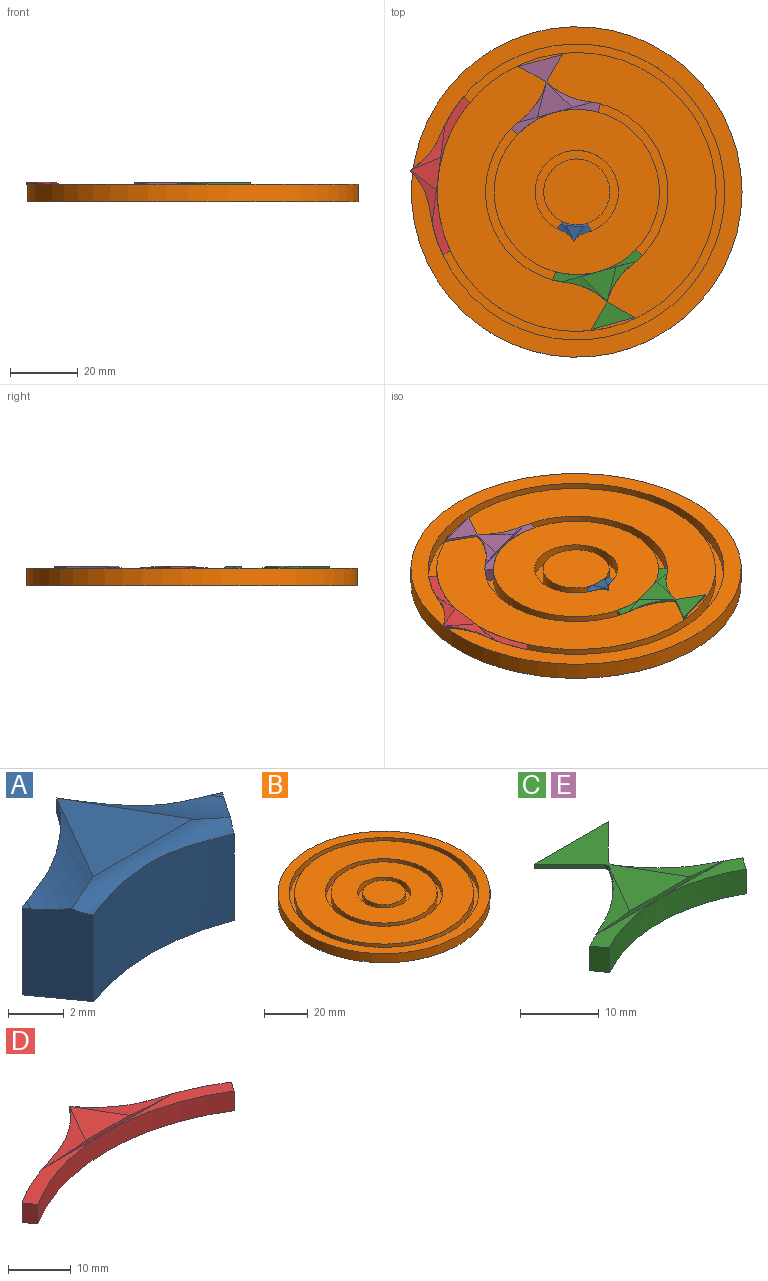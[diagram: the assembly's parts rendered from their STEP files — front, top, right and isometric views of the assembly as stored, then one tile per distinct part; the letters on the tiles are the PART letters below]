
ASSEMBLY  parts=5 mates=4
PART A: 16 faces, bbox 10.4x6.7x4.5 mm
  f0: plane 0.06x0.02mm, normal (0,0,1), area 0mm2, adj f4,f5,f15
  f1: plane 0.06x0.02mm, normal (0,0,1), area 0mm2, adj f3,f4,f15
  f2: plane 0.43x0.43mm, normal (0,0,1), area 0.1mm2, adj f5,f6,f12
  f3: plane 4.02x2.13mm, normal (-0.81,-0.59,0), area 10.1mm2, adj f1,f4,f6,f7,f8,f11,f15
  f4: cylinder r=9.75mm len=7.11mm, axis (0,0,-1), area 28.5mm2, adj f0,f1,f3,f5,f8,f15
  f5: plane 4.02x2.13mm, normal (0.81,-0.59,0), area 10.1mm2, adj f0,f2,f4,f6,f8,f12,f15
  f6: cylinder r=12.29mm len=10.16mm, axis (0,0,-1), area 40mm2, adj f2,f3,f5,f7,f8,f9,f11,f12
  f7: plane 0.43x0.43mm, normal (0,0,1), area 0.1mm2, adj f3,f6,f11
  f8: plane 10.16x3.21mm, normal (0,0,-1), area 22.6mm2, adj f3,f4,f5,f6
  f9: plane 7.33x2.78mm, normal (0,0,-1), area 5mm2, adj f6,f13,f14
  f10: plane 5.06x4.38mm, normal (0,0,1), area 11.1mm2, adj f11,f12,f15
  f11: cylinder r=5.08mm len=6.56mm, axis (-0.5,-0.87,0), area 6.3mm2, adj f3,f6,f7,f10,f13,f15
  f12: cylinder r=5.08mm len=6.56mm, axis (-0.5,0.87,0), area 6.3mm2, adj f2,f5,f6,f10,f14,f15
  f13: cylinder r=6.78mm len=3.67mm, axis (0,0,-1), area 1.7mm2, adj f6,f9,f11,f14
  f14: cylinder r=6.78mm len=3.67mm, axis (0,0,1), area 1.7mm2, adj f6,f9,f12,f13
  f15: cylinder r=1.17mm len=8.05mm, axis (1,0,0), area 5.9mm2, adj f0,f1,f3,f4,f5,f10,f11,f12
PART B: 15 faces, bbox 97.5x97.5x5.1 mm
  f0: cylinder r=48.77mm len=97.54mm, axis (0,0,-1), area 1556.6mm2, adj f1,f2
  f1: plane 97.54x97.54mm, normal (0,0,1), area 1475.5mm2, adj f0,f4
  f2: plane 97.54x97.54mm, normal (0,0,-1), area 7471.7mm2, adj f0
  f3: cylinder r=41.15mm len=82.3mm, axis (0,0,1), area 985mm2, adj f5,f6
  f4: cylinder r=43.69mm len=87.38mm, axis (0,0,1), area 1045.8mm2, adj f1,f5
  f5: plane 87.38x87.38mm, normal (0,0,1), area 677mm2, adj f3,f4
  f6: plane 82.3x82.3mm, normal (0,0,1), area 3041.9mm2, adj f3,f8
  f7: cylinder r=24.38mm len=48.77mm, axis (0,0,1), area 583.7mm2, adj f9,f10
  f8: cylinder r=26.92mm len=53.85mm, axis (0,0,1), area 644.5mm2, adj f6,f9
  f9: plane 53.85x53.85mm, normal (0,0,1), area 409.4mm2, adj f7,f8
  f10: plane 48.77x48.77mm, normal (0,0,1), area 1393.1mm2, adj f7,f12
  f11: cylinder r=9.75mm len=19.51mm, axis (0,0,1), area 233.5mm2, adj f13,f14
  f12: cylinder r=12.29mm len=24.59mm, axis (0,0,1), area 294.3mm2, adj f10,f13
  f13: plane 24.59x24.59mm, normal (0,0,1), area 175.9mm2, adj f11,f12
  f14: plane 19.51x19.51mm, normal (0,0,1), area 298.9mm2, adj f11
PART C: 19 faces, bbox 27.4x19.2x4.5 mm
  f0: cylinder r=20.82mm len=9.89mm, axis (0,0,-1), area 5.7mm2, adj f6,f9,f12,f14
  f1: cylinder r=20.82mm len=9.89mm, axis (0,0,1), area 5.7mm2, adj f6,f9,f13,f15
  f2: plane 13.72x3.29mm, normal (0,0,1), area 15mm2, adj f4,f5,f6,f10
  f3: plane 3.81x2.07mm, normal (-0.81,-0.59,0), area 9.7mm2, adj f4,f6,f7,f8
  f4: cylinder r=24.38mm len=24.45mm, axis (0,0,-1), area 97.6mm2, adj f2,f3,f5,f7,f8
  f5: plane 3.81x2.07mm, normal (0.81,-0.59,0), area 9.7mm2, adj f2,f4,f6,f8
  f6: cylinder r=26.92mm len=27.43mm, axis (0,0,-1), area 110mm2, adj f0,f1,f2,f3,f5,f7,f8,f9
  f7: plane 13.72x3.29mm, normal (0,0,1), area 15mm2, adj f3,f4,f6,f10
  f8: plane 27.43x5.83mm, normal (0,0,-1), area 69.1mm2, adj f3,f4,f5,f6
  f9: plane 20.2x15.32mm, normal (0,0,-1), area 85.6mm2, adj f0,f1,f6,f14,f15,f16,f17,f18
  f10: plane 22.84x0.64mm, normal (0,-1,0), area 10.6mm2, adj f2,f6,f7,f11,f12,f13
  f11: plane 15.88x13.29mm, normal (0,0,1), area 93.6mm2, adj f10,f12,f13,f14,f15,f16,f17,f18
  f12: cylinder r=53.59mm len=14.17mm, axis (-0.5,-0.87,0), area 15.7mm2, adj f0,f6,f10,f11
  f13: cylinder r=53.59mm len=14.17mm, axis (-0.5,0.87,0), area 15.7mm2, adj f1,f6,f10,f11
  f14: plane 0.64x0.64mm, normal (-0.99,-0.17,0), area 0.4mm2, adj f0,f9,f11,f18
  f15: plane 0.64x0.64mm, normal (0.99,-0.17,0), area 0.4mm2, adj f1,f9,f11,f16
  f16: plane 6.34x6.34mm, normal (0.71,-0.71,0), area 5.7mm2, adj f9,f11,f15,f17
  f17: plane 13.29x0.64mm, normal (0,1,0), area 8.4mm2, adj f9,f11,f16,f18
  f18: plane 6.34x6.34mm, normal (-0.71,-0.71,0), area 5.7mm2, adj f9,f11,f14,f17
PART D: 14 faces, bbox 47.1x19x4.5 mm
  f0: plane 23.55x6.54mm, normal (0,0,1), area 36.2mm2, adj f1,f2,f4,f8,f10
  f1: plane 3.81x2.06mm, normal (-0.81,-0.59,0), area 9.7mm2, adj f0,f2,f4,f6
  f2: cylinder r=41.15mm len=44.12mm, axis (0,0,-1), area 177.4mm2, adj f0,f1,f3,f5,f6
  f3: plane 3.81x2.06mm, normal (0.81,-0.59,0), area 9.7mm2, adj f2,f4,f5,f6
  f4: cylinder r=43.69mm len=47.1mm, axis (0,0,-1), area 189.6mm2, adj f0,f1,f3,f5,f6,f7,f10,f11
  f5: plane 23.55x6.54mm, normal (0,0,1), area 36.2mm2, adj f2,f3,f4,f8,f11
  f6: plane 47.1x8.95mm, normal (0,0,-1), area 122.3mm2, adj f1,f2,f3,f4
  f7: plane 22.32x7.4mm, normal (0,0,-1), area 41.1mm2, adj f4,f12,f13
  f8: plane 28.82x0.65mm, normal (0,-1,0), area 10.2mm2, adj f0,f5,f9,f10,f11
  f9: plane 9.81x8.49mm, normal (0,0,1), area 41.7mm2, adj f8,f10,f11
  f10: cylinder r=53.59mm len=16.72mm, axis (-0.5,-0.87,0), area 24.9mm2, adj f0,f4,f8,f9,f12
  f11: cylinder r=53.59mm len=16.72mm, axis (-0.5,0.87,0), area 24.9mm2, adj f4,f5,f8,f9,f13
  f12: cylinder r=20.82mm len=11.16mm, axis (0,0,-1), area 4.8mm2, adj f4,f7,f10,f13
  f13: cylinder r=20.82mm len=11.16mm, axis (0,0,1), area 4.8mm2, adj f4,f7,f11,f12
PART E: same geometry as C
PLACE A rot(axis=(0,0,1),176.4deg) t=(-24.59,-4.01,-2.54)mm
PLACE B t=(-24.59,-4.01,-2.54)mm fixed
PLACE C rot(axis=(0,0,-1),164.6deg) t=(-24.59,-4.01,-2.54)mm
PLACE D rot(axis=(0,0,1),82.5deg) t=(-24.59,-4.01,-2.54)mm
PLACE E rot(axis=(0,0,1),15.4deg) t=(-24.59,-4.01,-2.54)mm
MATE revolute D.f2 <-> B.f3  axis (0,0,-1) through (-24.59,-4.01,-1.27)mm
MATE revolute A.f4 <-> B.f11  axis (0,0,-1) through (-24.59,-4.01,-1.27)mm
MATE revolute C.f4 <-> B.f0  axis (0,0,-1) through (-24.59,-4.01,-1.27)mm
MATE revolute E.f4 <-> B.f7  axis (0,0,-1) through (-24.59,-4.01,-1.27)mm
